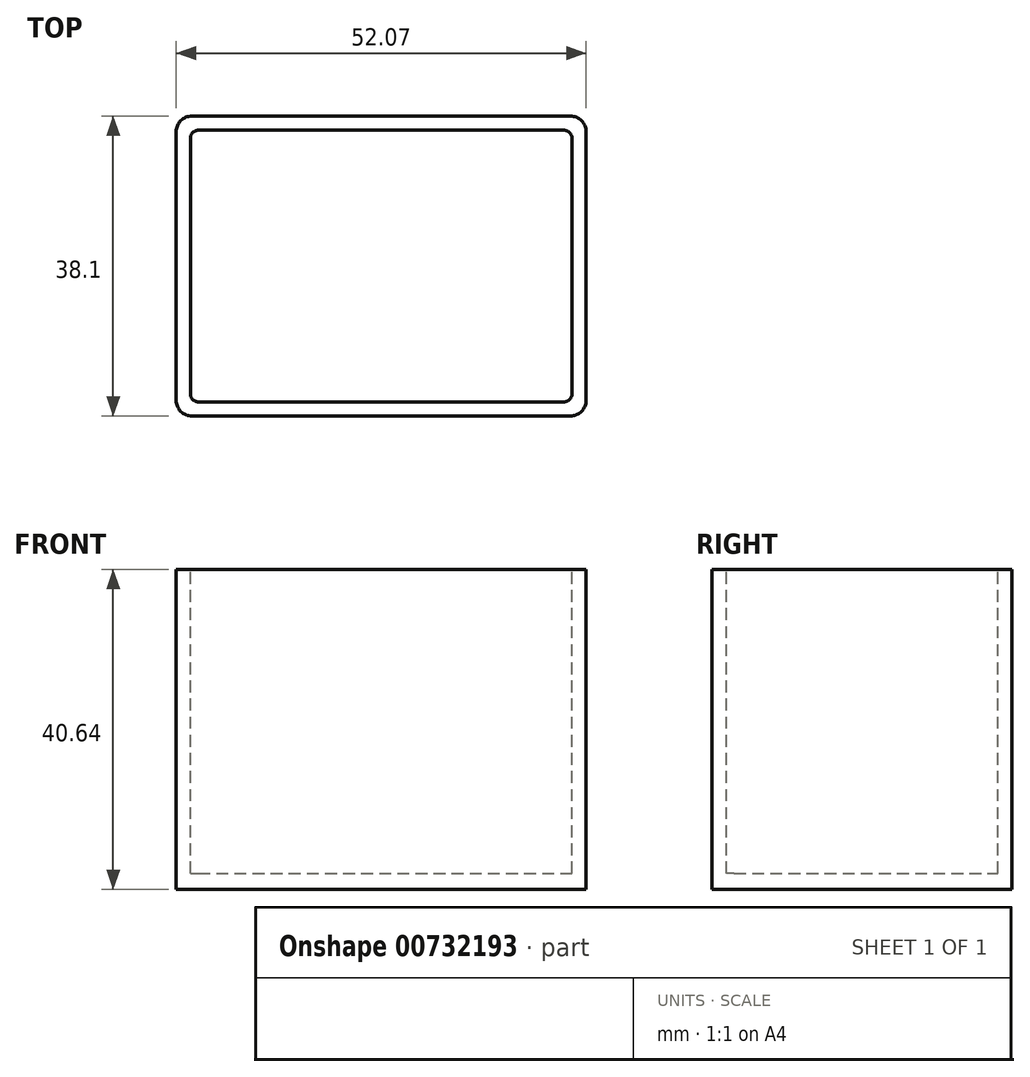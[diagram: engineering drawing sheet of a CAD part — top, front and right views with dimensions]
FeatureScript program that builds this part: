
annotation { "Feature Type Name" : "Feature", "Feature Type Description" : "" }
export const myFeature = defineFeature(function(context is Context, id is Id, definition is map)
    precondition{}
    {
        {
            var Q0;
            Q0=qCreatedBy(makeId("Top.planeOp"),FACE);
            var sketch = newSketch(context, id + "F0", { "sketchPlane" : qUnion([Q0])});
            skLineSegment(sketch, "E0.bottom", {"start": v(2, 0) * mm, "end": v(50.07, 0) * mm});
            skLineSegment(sketch, "E0.top", {"start": v(2, 38.1) * mm, "end": v(50.07, 38.1) * mm});
            skLineSegment(sketch, "E0.left", {"start": v(0, 2) * mm, "end": v(0, 36.1) * mm});
            skLineSegment(sketch, "E0.right", {"start": v(52.07, 2) * mm, "end": v(52.07, 36.1) * mm});
            skPoint(sketch, "E1.visualSharp", {"position": v(0, 38.1) * mm});
            skArc(sketch, "E1.filletArc", {"start": v(2, 38.1) * mm, "mid": v(0.59, 37.51) * mm, "end": v(0, 36.1) * mm});
            skPoint(sketch, "E2.visualSharp", {"position": v(52.07, 38.1) * mm});
            skArc(sketch, "E2.filletArc", {"start": v(52.07, 36.1) * mm, "mid": v(51.48, 37.51) * mm, "end": v(50.07, 38.1) * mm});
            skPoint(sketch, "E3.visualSharp", {"position": v(52.07, 0) * mm});
            skArc(sketch, "E3.filletArc", {"start": v(50.07, 0) * mm, "mid": v(51.48, 0.59) * mm, "end": v(52.07, 2) * mm});
            skPoint(sketch, "E4.visualSharp", {"position": v(0, 0) * mm});
            skArc(sketch, "E4.filletArc", {"start": v(0, 2) * mm, "mid": v(0.59, 0.59) * mm, "end": v(2, 0) * mm});
            skSolve(sketch);
        }
        {
            var Q0;
            Q0 = qSketchRegion(id + "F0", true);
            var Q1;
            Q1 = qSketchRegion(id + "F2", true);
            extrude(context, id + "F1", {"entities" : qUnion([Q0, Q1]), "depth" : 40.64 * mm, "offsetDistance" : 25 * mm});
        }
        {
            var Q0;
            Q0=makeQuery(id+"F1.opExtrude","CAP_FACE",FACE,{"disambiguationData":[OSD([sQuery(id+"F0.wireOp",EDGE,"E0.bottom"),sQuery(id+"F0.wireOp",EDGE,"E0.top"),sQuery(id+"F0.wireOp",EDGE,"E0.left"),sQuery(id+"F0.wireOp",EDGE,"E0.right"),sQuery(id+"F0.wireOp",EDGE,"E1.filletArc"),sQuery(id+"F0.wireOp",EDGE,"E2.filletArc"),sQuery(id+"F0.wireOp",EDGE,"E3.filletArc"),sQuery(id+"F0.wireOp",EDGE,"E4.filletArc")])],"isStart":false});
            var sketch = newSketch(context, id + "F2", { "sketchPlane" : qUnion([Q0])});
            skLineSegment(sketch, "E5.0", {"start": v(2, 38.1) * mm, "end": v(50.07, 38.1) * mm});
            skLineSegment(sketch, "E6.0", {"start": v(0, 2) * mm, "end": v(0, 36.1) * mm});
            skLineSegment(sketch, "E7.0", {"start": v(52.07, 2) * mm, "end": v(52.07, 36.1) * mm});
            skLineSegment(sketch, "E8.0", {"start": v(2, 0) * mm, "end": v(50.07, 0) * mm});
            skArc(sketch, "E9.0", {"start": v(2, 38.1) * mm, "mid": v(0.59, 37.51) * mm, "end": v(0, 36.1) * mm});
            skArc(sketch, "E10.0", {"start": v(52.07, 36.1) * mm, "mid": v(51.48, 37.51) * mm, "end": v(50.07, 38.1) * mm});
            skLineSegment(sketch, "E11.0", {"start": v(2.8, 36.3) * mm, "end": v(49.27, 36.3) * mm});
            skLineSegment(sketch, "E11.1", {"start": v(1.8, 2.8) * mm, "end": v(1.8, 35.3) * mm});
            skLineSegment(sketch, "E11.2", {"start": v(2.8, 1.8) * mm, "end": v(49.27, 1.8) * mm});
            skLineSegment(sketch, "E11.3", {"start": v(50.27, 2.8) * mm, "end": v(50.27, 35.3) * mm});
            skPoint(sketch, "E12.visualSharp", {"position": v(1.8, 36.3) * mm});
            skArc(sketch, "E12.filletArc", {"start": v(2.8, 36.3) * mm, "mid": v(2.1, 36) * mm, "end": v(1.8, 35.3) * mm});
            skPoint(sketch, "E13.visualSharp", {"position": v(1.8, 1.8) * mm});
            skArc(sketch, "E13.filletArc", {"start": v(1.8, 2.8) * mm, "mid": v(2.1, 2.1) * mm, "end": v(2.8, 1.8) * mm});
            skPoint(sketch, "E14.visualSharp", {"position": v(50.27, 1.8) * mm});
            skArc(sketch, "E14.filletArc", {"start": v(49.27, 1.8) * mm, "mid": v(49.98, 2.1) * mm, "end": v(50.27, 2.8) * mm});
            skPoint(sketch, "E15.visualSharp", {"position": v(50.27, 36.3) * mm});
            skArc(sketch, "E15.filletArc", {"start": v(50.27, 35.3) * mm, "mid": v(49.98, 36) * mm, "end": v(49.27, 36.3) * mm});
            skSolve(sketch);
        }
        {
            var Q0;
            Q0 = qSketchRegion(id + "F2", true);
            extrude(context, id + "F3", {"entities" : qUnion([Q0]), "operationType" : NewBodyOperationType.REMOVE, "oppositeDirection" : true, "depth" : 38.6 * mm, "offsetDistance" : 25.4 * mm});
        }
    });
